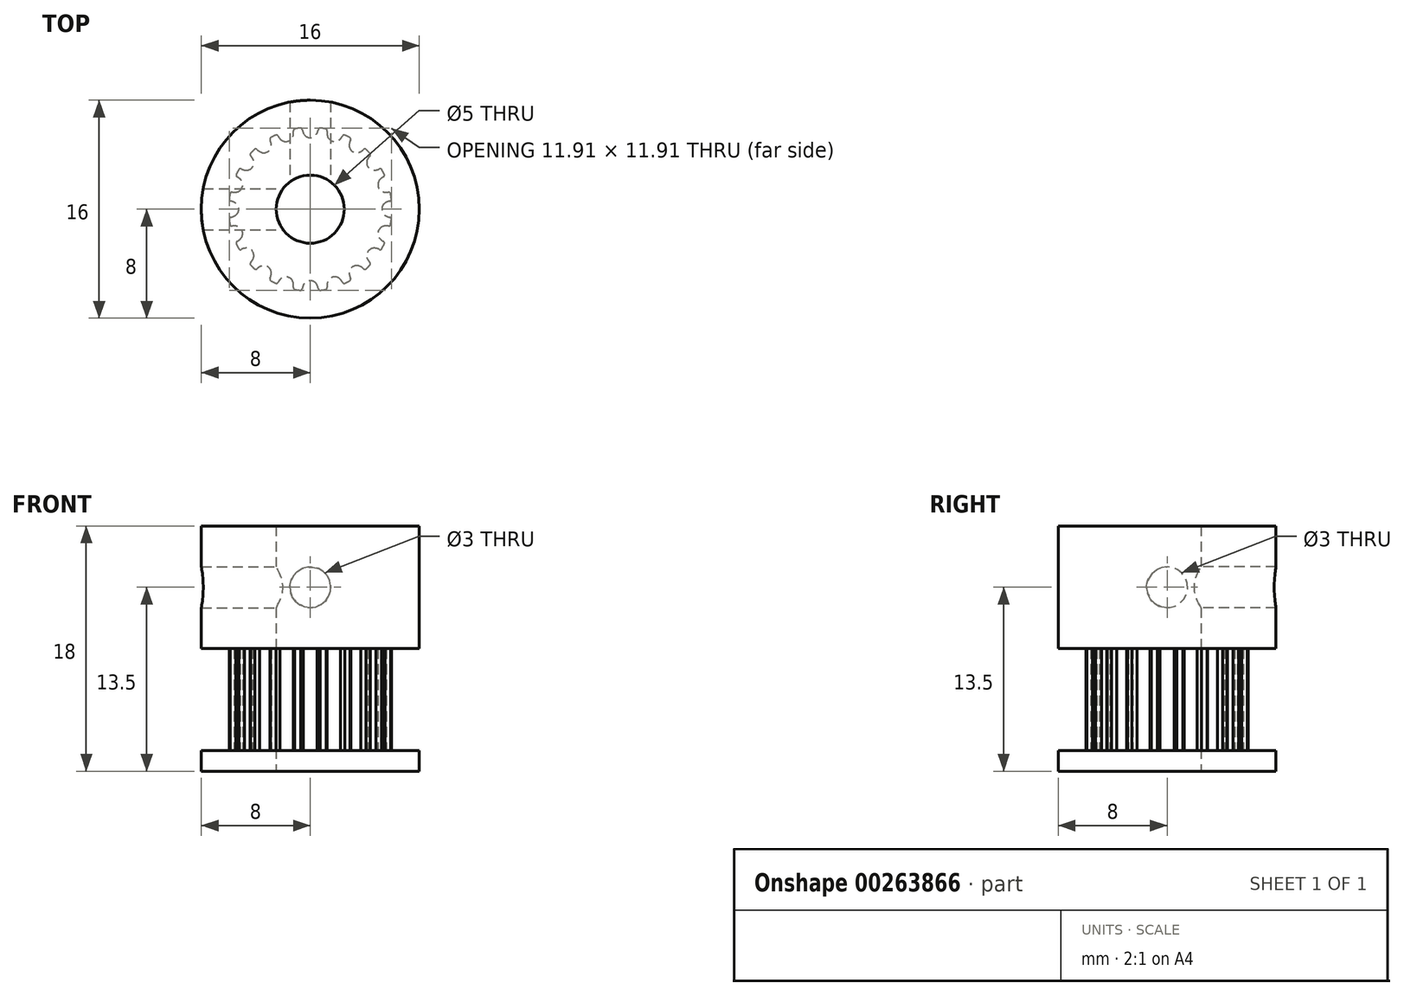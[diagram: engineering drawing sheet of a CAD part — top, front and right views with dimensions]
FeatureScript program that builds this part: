
annotation { "Feature Type Name" : "Feature", "Feature Type Description" : "" }
export const myFeature = defineFeature(function(context is Context, id is Id, definition is map)
    precondition{}
    {
        {
            var Q0;
            Q0=qCreatedBy(makeId("Top.planeOp"),FACE);
            var sketch = newSketch(context, id + "F0", { "sketchPlane" : qUnion([Q0])});
            skLineSegment(sketch, "E0", {"start": v(-19.17, 17.78) * mm, "end": v(-18.17, 17.78) * mm});
            skLineSegment(sketch, "E1", {"start": v(-18.17, 17.78) * mm, "end": v(-18.17, 18.4) * mm});
            skArc(sketch, "E2", {"start": v(-18.67, 18.85) * mm, "mid": v(-18.88, 19.07) * mm, "end": v(-19.17, 19.16) * mm});
            skArc(sketch, "E3", {"start": v(-18.58, 18.54) * mm, "mid": v(-18.61, 18.7) * mm, "end": v(-18.67, 18.85) * mm});
            skArc(sketch, "E4", {"start": v(-18.58, 18.54) * mm, "mid": v(-18.53, 18.44) * mm, "end": v(-18.43, 18.4) * mm});
            skLineSegment(sketch, "E5", {"start": v(-18.43, 18.4) * mm, "end": v(-18.17, 18.4) * mm});
            skArc(sketch, "E6.0.MirrorCS", {"start": v(-19.67, 18.85) * mm, "mid": v(-19.47, 19.07) * mm, "end": v(-19.17, 19.16) * mm});
            skArc(sketch, "E7.0.MirrorCS", {"start": v(-19.76, 18.54) * mm, "mid": v(-19.73, 18.7) * mm, "end": v(-19.67, 18.85) * mm});
            skArc(sketch, "E8.0.MirrorCS", {"start": v(-19.76, 18.54) * mm, "mid": v(-19.81, 18.44) * mm, "end": v(-19.91, 18.4) * mm});
            skLineSegment(sketch, "E9.0.MirrorCS", {"start": v(-19.91, 18.4) * mm, "end": v(-20.17, 18.4) * mm});
            skLineSegment(sketch, "E10.0.MirrorCS", {"start": v(-20.17, 17.78) * mm, "end": v(-20.17, 18.4) * mm});
            skLineSegment(sketch, "E11.0.MirrorCS", {"start": v(-19.17, 17.78) * mm, "end": v(-20.17, 17.78) * mm});
            skLineSegment(sketch, "E12.direction1", {"start": v(-20.17, 17.78) * mm, "end": v(-18.17, 17.78) * mm, "construction": true});
            skLineSegment(sketch, "E13", {"start": v(-20.17, 18.15) * mm, "end": v(-18.17, 18.15) * mm, "construction": true});
            skPoint(sketch, "E14", {"position": v(0, -5.25) * mm});
            skArc(sketch, "E15", {"start": v(0.51, -5.6) * mm, "mid": v(0, -5.25) * mm, "end": v(-0.51, -5.6) * mm});
            skArc(sketch, "E16", {"start": v(-0.51, -5.6) * mm, "mid": v(-0.56, -5.71) * mm, "end": v(-0.59, -5.83) * mm});
            skArc(sketch, "E17", {"start": v(0.59, -5.83) * mm, "mid": v(0.56, -5.71) * mm, "end": v(0.51, -5.6) * mm});
            skArc(sketch, "E18", {"start": v(0.72, -5.96) * mm, "mid": v(0.94, -5.93) * mm, "end": v(1.16, -5.89) * mm});
            skArc(sketch, "E19", {"start": v(0.59, -5.83) * mm, "mid": v(0.66, -5.94) * mm, "end": v(0.8, -5.95) * mm});
            skArc(sketch, "E20", {"start": v(-0.59, -5.83) * mm, "mid": v(-0.66, -5.94) * mm, "end": v(-0.8, -5.95) * mm});
            skArc(sketch, "E21.1.0", {"start": v(2.22, -5.16) * mm, "mid": v(1.62, -5) * mm, "end": v(1.24, -5.48) * mm});
            skPoint(sketch, "E21.1.1", {"position": v(1.62, -5) * mm});
            skArc(sketch, "E21.1.2", {"start": v(1.24, -5.48) * mm, "mid": v(1.23, -5.6) * mm, "end": v(1.24, -5.73) * mm});
            skArc(sketch, "E21.1.3", {"start": v(2.36, -5.37) * mm, "mid": v(2.47, -5.44) * mm, "end": v(2.6, -5.41) * mm});
            skArc(sketch, "E21.1.4", {"start": v(1.24, -5.73) * mm, "mid": v(1.2, -5.85) * mm, "end": v(1.08, -5.9) * mm});
            skArc(sketch, "E21.1.5", {"start": v(2.36, -5.37) * mm, "mid": v(2.3, -5.26) * mm, "end": v(2.22, -5.16) * mm});
            skArc(sketch, "E22.3.2.0", {"start": v(3.7, -4.22) * mm, "mid": v(3.09, -4.25) * mm, "end": v(2.87, -4.83) * mm});
            skPoint(sketch, "E22.4.2.0", {"position": v(3.09, -4.25) * mm});
            skArc(sketch, "E22.5.2.0", {"start": v(2.87, -4.83) * mm, "mid": v(2.9, -4.95) * mm, "end": v(2.95, -5.07) * mm});
            skArc(sketch, "E22.9.2.0", {"start": v(3.9, -4.37) * mm, "mid": v(4.03, -4.41) * mm, "end": v(4.14, -4.35) * mm});
            skArc(sketch, "E22.13.2.0", {"start": v(2.95, -5.07) * mm, "mid": v(2.95, -5.2) * mm, "end": v(2.85, -5.28) * mm});
            skArc(sketch, "E22.17.2.0", {"start": v(3.9, -4.37) * mm, "mid": v(3.81, -4.3) * mm, "end": v(3.7, -4.22) * mm});
            skArc(sketch, "E22.3.3.0", {"start": v(4.83, -2.87) * mm, "mid": v(4.25, -3.09) * mm, "end": v(4.22, -3.7) * mm});
            skPoint(sketch, "E22.4.3.0", {"position": v(4.25, -3.09) * mm});
            skArc(sketch, "E22.5.3.0", {"start": v(4.22, -3.7) * mm, "mid": v(4.3, -3.81) * mm, "end": v(4.37, -3.9) * mm});
            skArc(sketch, "E22.9.3.0", {"start": v(5.07, -2.95) * mm, "mid": v(5.2, -2.95) * mm, "end": v(5.28, -2.85) * mm});
            skArc(sketch, "E22.13.3.0", {"start": v(4.37, -3.9) * mm, "mid": v(4.41, -4.03) * mm, "end": v(4.35, -4.14) * mm});
            skArc(sketch, "E22.17.3.0", {"start": v(5.07, -2.95) * mm, "mid": v(4.95, -2.9) * mm, "end": v(4.83, -2.87) * mm});
            skArc(sketch, "E22.3.4.0", {"start": v(5.48, -1.24) * mm, "mid": v(5, -1.62) * mm, "end": v(5.16, -2.22) * mm});
            skPoint(sketch, "E22.4.4.0", {"position": v(5, -1.62) * mm});
            skArc(sketch, "E22.5.4.0", {"start": v(5.16, -2.22) * mm, "mid": v(5.26, -2.3) * mm, "end": v(5.37, -2.36) * mm});
            skArc(sketch, "E22.9.4.0", {"start": v(5.73, -1.24) * mm, "mid": v(5.85, -1.2) * mm, "end": v(5.9, -1.08) * mm});
            skArc(sketch, "E22.13.4.0", {"start": v(5.37, -2.36) * mm, "mid": v(5.44, -2.47) * mm, "end": v(5.41, -2.6) * mm});
            skArc(sketch, "E22.17.4.0", {"start": v(5.73, -1.24) * mm, "mid": v(5.6, -1.23) * mm, "end": v(5.48, -1.24) * mm});
            skArc(sketch, "E22.3.5.0", {"start": v(5.6, 0.51) * mm, "mid": v(5.25, 0) * mm, "end": v(5.6, -0.51) * mm});
            skPoint(sketch, "E22.4.5.0", {"position": v(5.25, 0) * mm});
            skArc(sketch, "E22.5.5.0", {"start": v(5.6, -0.51) * mm, "mid": v(5.71, -0.56) * mm, "end": v(5.83, -0.59) * mm});
            skArc(sketch, "E22.9.5.0", {"start": v(5.83, 0.59) * mm, "mid": v(5.94, 0.66) * mm, "end": v(5.95, 0.8) * mm});
            skArc(sketch, "E22.13.5.0", {"start": v(5.83, -0.59) * mm, "mid": v(5.94, -0.66) * mm, "end": v(5.95, -0.8) * mm});
            skArc(sketch, "E22.17.5.0", {"start": v(5.83, 0.59) * mm, "mid": v(5.71, 0.56) * mm, "end": v(5.6, 0.51) * mm});
            skArc(sketch, "E22.3.6.0", {"start": v(5.16, 2.22) * mm, "mid": v(5, 1.62) * mm, "end": v(5.48, 1.24) * mm});
            skPoint(sketch, "E22.4.6.0", {"position": v(5, 1.62) * mm});
            skArc(sketch, "E22.5.6.0", {"start": v(5.48, 1.24) * mm, "mid": v(5.6, 1.23) * mm, "end": v(5.73, 1.24) * mm});
            skArc(sketch, "E22.9.6.0", {"start": v(5.37, 2.36) * mm, "mid": v(5.44, 2.47) * mm, "end": v(5.41, 2.6) * mm});
            skArc(sketch, "E22.13.6.0", {"start": v(5.73, 1.24) * mm, "mid": v(5.85, 1.2) * mm, "end": v(5.9, 1.08) * mm});
            skArc(sketch, "E22.17.6.0", {"start": v(5.37, 2.36) * mm, "mid": v(5.26, 2.3) * mm, "end": v(5.16, 2.22) * mm});
            skArc(sketch, "E22.3.7.0", {"start": v(4.22, 3.7) * mm, "mid": v(4.25, 3.09) * mm, "end": v(4.83, 2.87) * mm});
            skPoint(sketch, "E22.4.7.0", {"position": v(4.25, 3.09) * mm});
            skArc(sketch, "E22.5.7.0", {"start": v(4.83, 2.87) * mm, "mid": v(4.95, 2.9) * mm, "end": v(5.07, 2.95) * mm});
            skArc(sketch, "E22.9.7.0", {"start": v(4.37, 3.9) * mm, "mid": v(4.41, 4.03) * mm, "end": v(4.35, 4.14) * mm});
            skArc(sketch, "E22.13.7.0", {"start": v(5.07, 2.95) * mm, "mid": v(5.2, 2.95) * mm, "end": v(5.28, 2.85) * mm});
            skArc(sketch, "E22.17.7.0", {"start": v(4.37, 3.9) * mm, "mid": v(4.3, 3.81) * mm, "end": v(4.22, 3.7) * mm});
            skArc(sketch, "E22.3.8.0", {"start": v(2.87, 4.83) * mm, "mid": v(3.09, 4.25) * mm, "end": v(3.7, 4.22) * mm});
            skPoint(sketch, "E22.4.8.0", {"position": v(3.09, 4.25) * mm});
            skArc(sketch, "E22.5.8.0", {"start": v(3.7, 4.22) * mm, "mid": v(3.81, 4.3) * mm, "end": v(3.9, 4.37) * mm});
            skArc(sketch, "E22.9.8.0", {"start": v(2.95, 5.07) * mm, "mid": v(2.95, 5.2) * mm, "end": v(2.85, 5.28) * mm});
            skArc(sketch, "E22.13.8.0", {"start": v(3.9, 4.37) * mm, "mid": v(4.03, 4.41) * mm, "end": v(4.14, 4.35) * mm});
            skArc(sketch, "E22.17.8.0", {"start": v(2.95, 5.07) * mm, "mid": v(2.9, 4.95) * mm, "end": v(2.87, 4.83) * mm});
            skArc(sketch, "E22.3.9.0", {"start": v(1.24, 5.48) * mm, "mid": v(1.62, 5) * mm, "end": v(2.22, 5.16) * mm});
            skPoint(sketch, "E22.4.9.0", {"position": v(1.62, 5) * mm});
            skArc(sketch, "E22.5.9.0", {"start": v(2.22, 5.16) * mm, "mid": v(2.3, 5.26) * mm, "end": v(2.36, 5.37) * mm});
            skArc(sketch, "E22.9.9.0", {"start": v(1.24, 5.73) * mm, "mid": v(1.2, 5.85) * mm, "end": v(1.08, 5.9) * mm});
            skArc(sketch, "E22.13.9.0", {"start": v(2.36, 5.37) * mm, "mid": v(2.47, 5.44) * mm, "end": v(2.6, 5.41) * mm});
            skArc(sketch, "E22.17.9.0", {"start": v(1.24, 5.73) * mm, "mid": v(1.23, 5.6) * mm, "end": v(1.24, 5.48) * mm});
            skArc(sketch, "E22.3.10.0", {"start": v(-0.51, 5.6) * mm, "mid": v(0, 5.25) * mm, "end": v(0.51, 5.6) * mm});
            skPoint(sketch, "E22.4.10.0", {"position": v(0, 5.25) * mm});
            skArc(sketch, "E22.5.10.0", {"start": v(0.51, 5.6) * mm, "mid": v(0.56, 5.71) * mm, "end": v(0.59, 5.83) * mm});
            skArc(sketch, "E22.9.10.0", {"start": v(-0.59, 5.83) * mm, "mid": v(-0.66, 5.94) * mm, "end": v(-0.8, 5.95) * mm});
            skArc(sketch, "E22.13.10.0", {"start": v(0.59, 5.83) * mm, "mid": v(0.66, 5.94) * mm, "end": v(0.8, 5.95) * mm});
            skArc(sketch, "E22.17.10.0", {"start": v(-0.59, 5.83) * mm, "mid": v(-0.56, 5.71) * mm, "end": v(-0.51, 5.6) * mm});
            skArc(sketch, "E22.3.11.0", {"start": v(-2.22, 5.16) * mm, "mid": v(-1.62, 5) * mm, "end": v(-1.24, 5.48) * mm});
            skPoint(sketch, "E22.4.11.0", {"position": v(-1.62, 5) * mm});
            skArc(sketch, "E22.5.11.0", {"start": v(-1.24, 5.48) * mm, "mid": v(-1.23, 5.6) * mm, "end": v(-1.24, 5.73) * mm});
            skArc(sketch, "E22.9.11.0", {"start": v(-2.36, 5.37) * mm, "mid": v(-2.47, 5.44) * mm, "end": v(-2.6, 5.41) * mm});
            skArc(sketch, "E22.13.11.0", {"start": v(-1.24, 5.73) * mm, "mid": v(-1.2, 5.85) * mm, "end": v(-1.08, 5.9) * mm});
            skArc(sketch, "E22.17.11.0", {"start": v(-2.36, 5.37) * mm, "mid": v(-2.3, 5.26) * mm, "end": v(-2.22, 5.16) * mm});
            skArc(sketch, "E22.3.12.0", {"start": v(-3.7, 4.22) * mm, "mid": v(-3.09, 4.25) * mm, "end": v(-2.87, 4.83) * mm});
            skPoint(sketch, "E22.4.12.0", {"position": v(-3.09, 4.25) * mm});
            skArc(sketch, "E22.5.12.0", {"start": v(-2.87, 4.83) * mm, "mid": v(-2.9, 4.95) * mm, "end": v(-2.95, 5.07) * mm});
            skArc(sketch, "E22.9.12.0", {"start": v(-3.9, 4.37) * mm, "mid": v(-4.03, 4.41) * mm, "end": v(-4.14, 4.35) * mm});
            skArc(sketch, "E22.13.12.0", {"start": v(-2.95, 5.07) * mm, "mid": v(-2.95, 5.2) * mm, "end": v(-2.85, 5.28) * mm});
            skArc(sketch, "E22.17.12.0", {"start": v(-3.9, 4.37) * mm, "mid": v(-3.81, 4.3) * mm, "end": v(-3.7, 4.22) * mm});
            skArc(sketch, "E22.3.13.0", {"start": v(-4.83, 2.87) * mm, "mid": v(-4.25, 3.09) * mm, "end": v(-4.22, 3.7) * mm});
            skPoint(sketch, "E22.4.13.0", {"position": v(-4.25, 3.09) * mm});
            skArc(sketch, "E22.5.13.0", {"start": v(-4.22, 3.7) * mm, "mid": v(-4.3, 3.81) * mm, "end": v(-4.37, 3.9) * mm});
            skArc(sketch, "E22.9.13.0", {"start": v(-5.07, 2.95) * mm, "mid": v(-5.2, 2.95) * mm, "end": v(-5.28, 2.85) * mm});
            skArc(sketch, "E22.13.13.0", {"start": v(-4.37, 3.9) * mm, "mid": v(-4.41, 4.03) * mm, "end": v(-4.35, 4.14) * mm});
            skArc(sketch, "E22.17.13.0", {"start": v(-5.07, 2.95) * mm, "mid": v(-4.95, 2.9) * mm, "end": v(-4.83, 2.87) * mm});
            skArc(sketch, "E22.3.14.0", {"start": v(-5.48, 1.24) * mm, "mid": v(-5, 1.62) * mm, "end": v(-5.16, 2.22) * mm});
            skPoint(sketch, "E22.4.14.0", {"position": v(-5, 1.62) * mm});
            skArc(sketch, "E22.5.14.0", {"start": v(-5.16, 2.22) * mm, "mid": v(-5.26, 2.3) * mm, "end": v(-5.37, 2.36) * mm});
            skArc(sketch, "E22.9.14.0", {"start": v(-5.73, 1.24) * mm, "mid": v(-5.85, 1.2) * mm, "end": v(-5.9, 1.08) * mm});
            skArc(sketch, "E22.13.14.0", {"start": v(-5.37, 2.36) * mm, "mid": v(-5.44, 2.47) * mm, "end": v(-5.41, 2.6) * mm});
            skArc(sketch, "E22.17.14.0", {"start": v(-5.73, 1.24) * mm, "mid": v(-5.6, 1.23) * mm, "end": v(-5.48, 1.24) * mm});
            skArc(sketch, "E22.3.15.0", {"start": v(-5.6, -0.51) * mm, "mid": v(-5.25, 0) * mm, "end": v(-5.6, 0.51) * mm});
            skPoint(sketch, "E22.4.15.0", {"position": v(-5.25, 0) * mm});
            skArc(sketch, "E22.5.15.0", {"start": v(-5.6, 0.51) * mm, "mid": v(-5.71, 0.56) * mm, "end": v(-5.83, 0.59) * mm});
            skArc(sketch, "E22.9.15.0", {"start": v(-5.83, -0.59) * mm, "mid": v(-5.94, -0.66) * mm, "end": v(-5.95, -0.8) * mm});
            skArc(sketch, "E22.13.15.0", {"start": v(-5.83, 0.59) * mm, "mid": v(-5.94, 0.66) * mm, "end": v(-5.95, 0.8) * mm});
            skArc(sketch, "E22.17.15.0", {"start": v(-5.83, -0.59) * mm, "mid": v(-5.71, -0.56) * mm, "end": v(-5.6, -0.51) * mm});
            skArc(sketch, "E22.3.16.0", {"start": v(-5.16, -2.22) * mm, "mid": v(-5, -1.62) * mm, "end": v(-5.48, -1.24) * mm});
            skPoint(sketch, "E22.4.16.0", {"position": v(-5, -1.62) * mm});
            skArc(sketch, "E22.5.16.0", {"start": v(-5.48, -1.24) * mm, "mid": v(-5.6, -1.23) * mm, "end": v(-5.73, -1.24) * mm});
            skArc(sketch, "E22.9.16.0", {"start": v(-5.37, -2.36) * mm, "mid": v(-5.44, -2.47) * mm, "end": v(-5.41, -2.6) * mm});
            skArc(sketch, "E22.13.16.0", {"start": v(-5.73, -1.24) * mm, "mid": v(-5.85, -1.2) * mm, "end": v(-5.9, -1.08) * mm});
            skArc(sketch, "E22.17.16.0", {"start": v(-5.37, -2.36) * mm, "mid": v(-5.26, -2.3) * mm, "end": v(-5.16, -2.22) * mm});
            skArc(sketch, "E22.3.17.0", {"start": v(-4.22, -3.7) * mm, "mid": v(-4.25, -3.09) * mm, "end": v(-4.83, -2.87) * mm});
            skPoint(sketch, "E22.4.17.0", {"position": v(-4.25, -3.09) * mm});
            skArc(sketch, "E22.5.17.0", {"start": v(-4.83, -2.87) * mm, "mid": v(-4.95, -2.9) * mm, "end": v(-5.07, -2.95) * mm});
            skArc(sketch, "E22.9.17.0", {"start": v(-4.37, -3.9) * mm, "mid": v(-4.41, -4.03) * mm, "end": v(-4.35, -4.14) * mm});
            skArc(sketch, "E22.13.17.0", {"start": v(-5.07, -2.95) * mm, "mid": v(-5.2, -2.95) * mm, "end": v(-5.28, -2.85) * mm});
            skArc(sketch, "E22.17.17.0", {"start": v(-4.37, -3.9) * mm, "mid": v(-4.3, -3.81) * mm, "end": v(-4.22, -3.7) * mm});
            skArc(sketch, "E22.3.18.0", {"start": v(-2.87, -4.83) * mm, "mid": v(-3.09, -4.25) * mm, "end": v(-3.7, -4.22) * mm});
            skPoint(sketch, "E22.4.18.0", {"position": v(-3.09, -4.25) * mm});
            skArc(sketch, "E22.5.18.0", {"start": v(-3.7, -4.22) * mm, "mid": v(-3.81, -4.3) * mm, "end": v(-3.9, -4.37) * mm});
            skArc(sketch, "E22.9.18.0", {"start": v(-2.95, -5.07) * mm, "mid": v(-2.95, -5.2) * mm, "end": v(-2.85, -5.28) * mm});
            skArc(sketch, "E22.13.18.0", {"start": v(-3.9, -4.37) * mm, "mid": v(-4.03, -4.41) * mm, "end": v(-4.14, -4.35) * mm});
            skArc(sketch, "E22.17.18.0", {"start": v(-2.95, -5.07) * mm, "mid": v(-2.9, -4.95) * mm, "end": v(-2.87, -4.83) * mm});
            skArc(sketch, "E22.3.19.0", {"start": v(-1.24, -5.48) * mm, "mid": v(-1.62, -5) * mm, "end": v(-2.22, -5.16) * mm});
            skPoint(sketch, "E22.4.19.0", {"position": v(-1.62, -5) * mm});
            skArc(sketch, "E22.5.19.0", {"start": v(-2.22, -5.16) * mm, "mid": v(-2.3, -5.26) * mm, "end": v(-2.36, -5.37) * mm});
            skArc(sketch, "E22.9.19.0", {"start": v(-1.24, -5.73) * mm, "mid": v(-1.2, -5.85) * mm, "end": v(-1.08, -5.9) * mm});
            skArc(sketch, "E22.13.19.0", {"start": v(-2.36, -5.37) * mm, "mid": v(-2.47, -5.44) * mm, "end": v(-2.6, -5.41) * mm});
            skArc(sketch, "E22.17.19.0", {"start": v(-1.24, -5.73) * mm, "mid": v(-1.23, -5.6) * mm, "end": v(-1.24, -5.48) * mm});
            skArc(sketch, "E23.trimOffspring", {"start": v(2.52, -5.44) * mm, "mid": v(2.72, -5.35) * mm, "end": v(2.92, -5.24) * mm});
            skArc(sketch, "E24.trimOffspring", {"start": v(4.08, -4.4) * mm, "mid": v(4.24, -4.24) * mm, "end": v(4.4, -4.08) * mm});
            skArc(sketch, "E25.trimOffspring", {"start": v(5.24, -2.92) * mm, "mid": v(5.33, -2.76) * mm, "end": v(5.41, -2.6) * mm});
            skArc(sketch, "E26.trimOffspring", {"start": v(5.89, -1.16) * mm, "mid": v(5.93, -0.94) * mm, "end": v(5.96, -0.72) * mm});
            skArc(sketch, "E27.trimOffspring", {"start": v(5.44, 2.52) * mm, "mid": v(5.35, 2.72) * mm, "end": v(5.24, 2.92) * mm});
            skArc(sketch, "E28.trimOffspring", {"start": v(4.4, 4.08) * mm, "mid": v(4.24, 4.24) * mm, "end": v(4.08, 4.4) * mm});
            skArc(sketch, "E29.trimOffspring", {"start": v(5.96, 0.72) * mm, "mid": v(5.93, 0.94) * mm, "end": v(5.89, 1.16) * mm});
            skArc(sketch, "E30.trimOffspring", {"start": v(2.92, 5.24) * mm, "mid": v(2.72, 5.35) * mm, "end": v(2.52, 5.44) * mm});
            skArc(sketch, "E31.trimOffspring", {"start": v(1.16, 5.89) * mm, "mid": v(0.94, 5.93) * mm, "end": v(0.72, 5.96) * mm});
            skArc(sketch, "E32.trimOffspring", {"start": v(-0.72, 5.96) * mm, "mid": v(-0.94, 5.93) * mm, "end": v(-1.16, 5.89) * mm});
            skArc(sketch, "E33.trimOffspring", {"start": v(-2.52, 5.44) * mm, "mid": v(-2.72, 5.35) * mm, "end": v(-2.92, 5.24) * mm});
            skArc(sketch, "E34.trimOffspring", {"start": v(-4.08, 4.4) * mm, "mid": v(-4.24, 4.24) * mm, "end": v(-4.4, 4.08) * mm});
            skArc(sketch, "E35.trimOffspring", {"start": v(-5.24, 2.92) * mm, "mid": v(-5.35, 2.72) * mm, "end": v(-5.44, 2.52) * mm});
            skArc(sketch, "E36.trimOffspring", {"start": v(-5.89, 1.16) * mm, "mid": v(-5.93, 0.94) * mm, "end": v(-5.96, 0.72) * mm});
            skArc(sketch, "E37.trimOffspring", {"start": v(-5.96, -0.72) * mm, "mid": v(-5.93, -0.94) * mm, "end": v(-5.89, -1.16) * mm});
            skArc(sketch, "E38.trimOffspring", {"start": v(-5.44, -2.52) * mm, "mid": v(-5.35, -2.72) * mm, "end": v(-5.24, -2.92) * mm});
            skArc(sketch, "E39.trimOffspring", {"start": v(-4.4, -4.08) * mm, "mid": v(-4.24, -4.24) * mm, "end": v(-4.08, -4.4) * mm});
            skArc(sketch, "E40.trimOffspring", {"start": v(-2.92, -5.24) * mm, "mid": v(-2.72, -5.35) * mm, "end": v(-2.52, -5.44) * mm});
            skArc(sketch, "E41.trimOffspring", {"start": v(-1.16, -5.89) * mm, "mid": v(-0.94, -5.93) * mm, "end": v(-0.72, -5.96) * mm});
            skSolve(sketch);
        }
        {
            var Q0;
            Q0=makeQuery(id+"F0.imprint","IMPRINT",FACE,{"disambiguationData":[TD([[makeQuery(id+"F0.imprint","IMPRINT",EDGE,{"derivedFrom":sQuery(id+"F0.wireOp",EDGE,"E15")}),-1.0]])]});
            extrude(context, id + "F1", {"entities" : qUnion([Q0]), "depth" : 7.5 * mm});
        }
        {
            var Q0;
            Q0=makeQuery(id+"F1.opExtrude","CAP_FACE",FACE,{"disambiguationData":[OSD([sQuery(id+"F0.wireOp",EDGE,"E15"),sQuery(id+"F0.wireOp",EDGE,"E16"),sQuery(id+"F0.wireOp",EDGE,"E17"),sQuery(id+"F0.wireOp",EDGE,"E18"),sQuery(id+"F0.wireOp",EDGE,"E19"),sQuery(id+"F0.wireOp",EDGE,"E20"),sQuery(id+"F0.wireOp",EDGE,"E21.1.0"),sQuery(id+"F0.wireOp",EDGE,"E21.1.2"),sQuery(id+"F0.wireOp",EDGE,"E21.1.3"),sQuery(id+"F0.wireOp",EDGE,"E21.1.4"),sQuery(id+"F0.wireOp",EDGE,"E21.1.5"),sQuery(id+"F0.wireOp",EDGE,"E22.3.2.0"),sQuery(id+"F0.wireOp",EDGE,"E22.5.2.0"),sQuery(id+"F0.wireOp",EDGE,"E22.9.2.0"),sQuery(id+"F0.wireOp",EDGE,"E22.13.2.0"),sQuery(id+"F0.wireOp",EDGE,"E22.17.2.0"),sQuery(id+"F0.wireOp",EDGE,"E22.3.3.0"),sQuery(id+"F0.wireOp",EDGE,"E22.5.3.0"),sQuery(id+"F0.wireOp",EDGE,"E22.9.3.0"),sQuery(id+"F0.wireOp",EDGE,"E22.13.3.0"),sQuery(id+"F0.wireOp",EDGE,"E22.17.3.0"),sQuery(id+"F0.wireOp",EDGE,"E22.3.4.0"),sQuery(id+"F0.wireOp",EDGE,"E22.5.4.0"),sQuery(id+"F0.wireOp",EDGE,"E22.9.4.0"),sQuery(id+"F0.wireOp",EDGE,"E22.13.4.0"),sQuery(id+"F0.wireOp",EDGE,"E22.17.4.0"),sQuery(id+"F0.wireOp",EDGE,"E22.3.5.0"),sQuery(id+"F0.wireOp",EDGE,"E22.5.5.0"),sQuery(id+"F0.wireOp",EDGE,"E22.9.5.0"),sQuery(id+"F0.wireOp",EDGE,"E22.13.5.0"),sQuery(id+"F0.wireOp",EDGE,"E22.17.5.0"),sQuery(id+"F0.wireOp",EDGE,"E22.3.6.0"),sQuery(id+"F0.wireOp",EDGE,"E22.5.6.0"),sQuery(id+"F0.wireOp",EDGE,"E22.9.6.0"),sQuery(id+"F0.wireOp",EDGE,"E22.13.6.0"),sQuery(id+"F0.wireOp",EDGE,"E22.17.6.0"),sQuery(id+"F0.wireOp",EDGE,"E22.3.7.0"),sQuery(id+"F0.wireOp",EDGE,"E22.5.7.0"),sQuery(id+"F0.wireOp",EDGE,"E22.9.7.0"),sQuery(id+"F0.wireOp",EDGE,"E22.13.7.0"),sQuery(id+"F0.wireOp",EDGE,"E22.17.7.0"),sQuery(id+"F0.wireOp",EDGE,"E22.3.8.0"),sQuery(id+"F0.wireOp",EDGE,"E22.5.8.0"),sQuery(id+"F0.wireOp",EDGE,"E22.9.8.0"),sQuery(id+"F0.wireOp",EDGE,"E22.13.8.0"),sQuery(id+"F0.wireOp",EDGE,"E22.17.8.0"),sQuery(id+"F0.wireOp",EDGE,"E22.3.9.0"),sQuery(id+"F0.wireOp",EDGE,"E22.5.9.0"),sQuery(id+"F0.wireOp",EDGE,"E22.9.9.0"),sQuery(id+"F0.wireOp",EDGE,"E22.13.9.0"),sQuery(id+"F0.wireOp",EDGE,"E22.17.9.0"),sQuery(id+"F0.wireOp",EDGE,"E22.3.10.0"),sQuery(id+"F0.wireOp",EDGE,"E22.5.10.0"),sQuery(id+"F0.wireOp",EDGE,"E22.9.10.0"),sQuery(id+"F0.wireOp",EDGE,"E22.13.10.0"),sQuery(id+"F0.wireOp",EDGE,"E22.17.10.0"),sQuery(id+"F0.wireOp",EDGE,"E22.3.11.0"),sQuery(id+"F0.wireOp",EDGE,"E22.5.11.0"),sQuery(id+"F0.wireOp",EDGE,"E22.9.11.0"),sQuery(id+"F0.wireOp",EDGE,"E22.13.11.0"),sQuery(id+"F0.wireOp",EDGE,"E22.17.11.0"),sQuery(id+"F0.wireOp",EDGE,"E22.3.12.0"),sQuery(id+"F0.wireOp",EDGE,"E22.5.12.0"),sQuery(id+"F0.wireOp",EDGE,"E22.9.12.0"),sQuery(id+"F0.wireOp",EDGE,"E22.13.12.0"),sQuery(id+"F0.wireOp",EDGE,"E22.17.12.0"),sQuery(id+"F0.wireOp",EDGE,"E22.3.13.0"),sQuery(id+"F0.wireOp",EDGE,"E22.5.13.0"),sQuery(id+"F0.wireOp",EDGE,"E22.9.13.0"),sQuery(id+"F0.wireOp",EDGE,"E22.13.13.0"),sQuery(id+"F0.wireOp",EDGE,"E22.17.13.0"),sQuery(id+"F0.wireOp",EDGE,"E22.3.14.0"),sQuery(id+"F0.wireOp",EDGE,"E22.5.14.0"),sQuery(id+"F0.wireOp",EDGE,"E22.9.14.0"),sQuery(id+"F0.wireOp",EDGE,"E22.13.14.0"),sQuery(id+"F0.wireOp",EDGE,"E22.17.14.0"),sQuery(id+"F0.wireOp",EDGE,"E22.3.15.0"),sQuery(id+"F0.wireOp",EDGE,"E22.5.15.0"),sQuery(id+"F0.wireOp",EDGE,"E22.9.15.0"),sQuery(id+"F0.wireOp",EDGE,"E22.13.15.0"),sQuery(id+"F0.wireOp",EDGE,"E22.17.15.0"),sQuery(id+"F0.wireOp",EDGE,"E22.3.16.0"),sQuery(id+"F0.wireOp",EDGE,"E22.5.16.0"),sQuery(id+"F0.wireOp",EDGE,"E22.9.16.0"),sQuery(id+"F0.wireOp",EDGE,"E22.13.16.0"),sQuery(id+"F0.wireOp",EDGE,"E22.17.16.0"),sQuery(id+"F0.wireOp",EDGE,"E22.3.17.0"),sQuery(id+"F0.wireOp",EDGE,"E22.5.17.0"),sQuery(id+"F0.wireOp",EDGE,"E22.9.17.0"),sQuery(id+"F0.wireOp",EDGE,"E22.13.17.0"),sQuery(id+"F0.wireOp",EDGE,"E22.17.17.0"),sQuery(id+"F0.wireOp",EDGE,"E22.3.18.0"),sQuery(id+"F0.wireOp",EDGE,"E22.5.18.0"),sQuery(id+"F0.wireOp",EDGE,"E22.9.18.0"),sQuery(id+"F0.wireOp",EDGE,"E22.13.18.0"),sQuery(id+"F0.wireOp",EDGE,"E22.17.18.0"),sQuery(id+"F0.wireOp",EDGE,"E22.3.19.0"),sQuery(id+"F0.wireOp",EDGE,"E22.5.19.0"),sQuery(id+"F0.wireOp",EDGE,"E22.9.19.0"),sQuery(id+"F0.wireOp",EDGE,"E22.13.19.0"),sQuery(id+"F0.wireOp",EDGE,"E22.17.19.0"),sQuery(id+"F0.wireOp",EDGE,"E23.trimOffspring"),sQuery(id+"F0.wireOp",EDGE,"E24.trimOffspring"),sQuery(id+"F0.wireOp",EDGE,"E25.trimOffspring"),sQuery(id+"F0.wireOp",EDGE,"E26.trimOffspring"),sQuery(id+"F0.wireOp",EDGE,"E27.trimOffspring"),sQuery(id+"F0.wireOp",EDGE,"E28.trimOffspring"),sQuery(id+"F0.wireOp",EDGE,"E29.trimOffspring"),sQuery(id+"F0.wireOp",EDGE,"E30.trimOffspring"),sQuery(id+"F0.wireOp",EDGE,"E31.trimOffspring"),sQuery(id+"F0.wireOp",EDGE,"E32.trimOffspring"),sQuery(id+"F0.wireOp",EDGE,"E33.trimOffspring"),sQuery(id+"F0.wireOp",EDGE,"E34.trimOffspring"),sQuery(id+"F0.wireOp",EDGE,"E35.trimOffspring"),sQuery(id+"F0.wireOp",EDGE,"E36.trimOffspring"),sQuery(id+"F0.wireOp",EDGE,"E37.trimOffspring"),sQuery(id+"F0.wireOp",EDGE,"E38.trimOffspring"),sQuery(id+"F0.wireOp",EDGE,"E39.trimOffspring"),sQuery(id+"F0.wireOp",EDGE,"E40.trimOffspring"),sQuery(id+"F0.wireOp",EDGE,"E41.trimOffspring")])],"isStart":false});
            var sketch = newSketch(context, id + "F2", { "sketchPlane" : qUnion([Q0])});
            skCircle(sketch, "E42", {"center": v(0, 0) * mm, "radius": 8 * mm});
            skSolve(sketch);
        }
        {
            var Q0;
            Q0=qSketchRegion(id+"F2",true);
            extrude(context, id + "F3", {"entities" : qUnion([Q0]), "operationType" : NewBodyOperationType.ADD, "depth" : 9 * mm});
        }
        {
            var Q0;
            Q0=makeQuery(id+"F1.opExtrude","CAP_FACE",FACE,{"disambiguationData":[OSD([sQuery(id+"F0.wireOp",EDGE,"E15"),sQuery(id+"F0.wireOp",EDGE,"E16"),sQuery(id+"F0.wireOp",EDGE,"E17"),sQuery(id+"F0.wireOp",EDGE,"E18"),sQuery(id+"F0.wireOp",EDGE,"E19"),sQuery(id+"F0.wireOp",EDGE,"E20"),sQuery(id+"F0.wireOp",EDGE,"E21.1.0"),sQuery(id+"F0.wireOp",EDGE,"E21.1.2"),sQuery(id+"F0.wireOp",EDGE,"E21.1.3"),sQuery(id+"F0.wireOp",EDGE,"E21.1.4"),sQuery(id+"F0.wireOp",EDGE,"E21.1.5"),sQuery(id+"F0.wireOp",EDGE,"E22.3.2.0"),sQuery(id+"F0.wireOp",EDGE,"E22.5.2.0"),sQuery(id+"F0.wireOp",EDGE,"E22.9.2.0"),sQuery(id+"F0.wireOp",EDGE,"E22.13.2.0"),sQuery(id+"F0.wireOp",EDGE,"E22.17.2.0"),sQuery(id+"F0.wireOp",EDGE,"E22.3.3.0"),sQuery(id+"F0.wireOp",EDGE,"E22.5.3.0"),sQuery(id+"F0.wireOp",EDGE,"E22.9.3.0"),sQuery(id+"F0.wireOp",EDGE,"E22.13.3.0"),sQuery(id+"F0.wireOp",EDGE,"E22.17.3.0"),sQuery(id+"F0.wireOp",EDGE,"E22.3.4.0"),sQuery(id+"F0.wireOp",EDGE,"E22.5.4.0"),sQuery(id+"F0.wireOp",EDGE,"E22.9.4.0"),sQuery(id+"F0.wireOp",EDGE,"E22.13.4.0"),sQuery(id+"F0.wireOp",EDGE,"E22.17.4.0"),sQuery(id+"F0.wireOp",EDGE,"E22.3.5.0"),sQuery(id+"F0.wireOp",EDGE,"E22.5.5.0"),sQuery(id+"F0.wireOp",EDGE,"E22.9.5.0"),sQuery(id+"F0.wireOp",EDGE,"E22.13.5.0"),sQuery(id+"F0.wireOp",EDGE,"E22.17.5.0"),sQuery(id+"F0.wireOp",EDGE,"E22.3.6.0"),sQuery(id+"F0.wireOp",EDGE,"E22.5.6.0"),sQuery(id+"F0.wireOp",EDGE,"E22.9.6.0"),sQuery(id+"F0.wireOp",EDGE,"E22.13.6.0"),sQuery(id+"F0.wireOp",EDGE,"E22.17.6.0"),sQuery(id+"F0.wireOp",EDGE,"E22.3.7.0"),sQuery(id+"F0.wireOp",EDGE,"E22.5.7.0"),sQuery(id+"F0.wireOp",EDGE,"E22.9.7.0"),sQuery(id+"F0.wireOp",EDGE,"E22.13.7.0"),sQuery(id+"F0.wireOp",EDGE,"E22.17.7.0"),sQuery(id+"F0.wireOp",EDGE,"E22.3.8.0"),sQuery(id+"F0.wireOp",EDGE,"E22.5.8.0"),sQuery(id+"F0.wireOp",EDGE,"E22.9.8.0"),sQuery(id+"F0.wireOp",EDGE,"E22.13.8.0"),sQuery(id+"F0.wireOp",EDGE,"E22.17.8.0"),sQuery(id+"F0.wireOp",EDGE,"E22.3.9.0"),sQuery(id+"F0.wireOp",EDGE,"E22.5.9.0"),sQuery(id+"F0.wireOp",EDGE,"E22.9.9.0"),sQuery(id+"F0.wireOp",EDGE,"E22.13.9.0"),sQuery(id+"F0.wireOp",EDGE,"E22.17.9.0"),sQuery(id+"F0.wireOp",EDGE,"E22.3.10.0"),sQuery(id+"F0.wireOp",EDGE,"E22.5.10.0"),sQuery(id+"F0.wireOp",EDGE,"E22.9.10.0"),sQuery(id+"F0.wireOp",EDGE,"E22.13.10.0"),sQuery(id+"F0.wireOp",EDGE,"E22.17.10.0"),sQuery(id+"F0.wireOp",EDGE,"E22.3.11.0"),sQuery(id+"F0.wireOp",EDGE,"E22.5.11.0"),sQuery(id+"F0.wireOp",EDGE,"E22.9.11.0"),sQuery(id+"F0.wireOp",EDGE,"E22.13.11.0"),sQuery(id+"F0.wireOp",EDGE,"E22.17.11.0"),sQuery(id+"F0.wireOp",EDGE,"E22.3.12.0"),sQuery(id+"F0.wireOp",EDGE,"E22.5.12.0"),sQuery(id+"F0.wireOp",EDGE,"E22.9.12.0"),sQuery(id+"F0.wireOp",EDGE,"E22.13.12.0"),sQuery(id+"F0.wireOp",EDGE,"E22.17.12.0"),sQuery(id+"F0.wireOp",EDGE,"E22.3.13.0"),sQuery(id+"F0.wireOp",EDGE,"E22.5.13.0"),sQuery(id+"F0.wireOp",EDGE,"E22.9.13.0"),sQuery(id+"F0.wireOp",EDGE,"E22.13.13.0"),sQuery(id+"F0.wireOp",EDGE,"E22.17.13.0"),sQuery(id+"F0.wireOp",EDGE,"E22.3.14.0"),sQuery(id+"F0.wireOp",EDGE,"E22.5.14.0"),sQuery(id+"F0.wireOp",EDGE,"E22.9.14.0"),sQuery(id+"F0.wireOp",EDGE,"E22.13.14.0"),sQuery(id+"F0.wireOp",EDGE,"E22.17.14.0"),sQuery(id+"F0.wireOp",EDGE,"E22.3.15.0"),sQuery(id+"F0.wireOp",EDGE,"E22.5.15.0"),sQuery(id+"F0.wireOp",EDGE,"E22.9.15.0"),sQuery(id+"F0.wireOp",EDGE,"E22.13.15.0"),sQuery(id+"F0.wireOp",EDGE,"E22.17.15.0"),sQuery(id+"F0.wireOp",EDGE,"E22.3.16.0"),sQuery(id+"F0.wireOp",EDGE,"E22.5.16.0"),sQuery(id+"F0.wireOp",EDGE,"E22.9.16.0"),sQuery(id+"F0.wireOp",EDGE,"E22.13.16.0"),sQuery(id+"F0.wireOp",EDGE,"E22.17.16.0"),sQuery(id+"F0.wireOp",EDGE,"E22.3.17.0"),sQuery(id+"F0.wireOp",EDGE,"E22.5.17.0"),sQuery(id+"F0.wireOp",EDGE,"E22.9.17.0"),sQuery(id+"F0.wireOp",EDGE,"E22.13.17.0"),sQuery(id+"F0.wireOp",EDGE,"E22.17.17.0"),sQuery(id+"F0.wireOp",EDGE,"E22.3.18.0"),sQuery(id+"F0.wireOp",EDGE,"E22.5.18.0"),sQuery(id+"F0.wireOp",EDGE,"E22.9.18.0"),sQuery(id+"F0.wireOp",EDGE,"E22.13.18.0"),sQuery(id+"F0.wireOp",EDGE,"E22.17.18.0"),sQuery(id+"F0.wireOp",EDGE,"E22.3.19.0"),sQuery(id+"F0.wireOp",EDGE,"E22.5.19.0"),sQuery(id+"F0.wireOp",EDGE,"E22.9.19.0"),sQuery(id+"F0.wireOp",EDGE,"E22.13.19.0"),sQuery(id+"F0.wireOp",EDGE,"E22.17.19.0"),sQuery(id+"F0.wireOp",EDGE,"E23.trimOffspring"),sQuery(id+"F0.wireOp",EDGE,"E24.trimOffspring"),sQuery(id+"F0.wireOp",EDGE,"E25.trimOffspring"),sQuery(id+"F0.wireOp",EDGE,"E26.trimOffspring"),sQuery(id+"F0.wireOp",EDGE,"E27.trimOffspring"),sQuery(id+"F0.wireOp",EDGE,"E28.trimOffspring"),sQuery(id+"F0.wireOp",EDGE,"E29.trimOffspring"),sQuery(id+"F0.wireOp",EDGE,"E30.trimOffspring"),sQuery(id+"F0.wireOp",EDGE,"E31.trimOffspring"),sQuery(id+"F0.wireOp",EDGE,"E32.trimOffspring"),sQuery(id+"F0.wireOp",EDGE,"E33.trimOffspring"),sQuery(id+"F0.wireOp",EDGE,"E34.trimOffspring"),sQuery(id+"F0.wireOp",EDGE,"E35.trimOffspring"),sQuery(id+"F0.wireOp",EDGE,"E36.trimOffspring"),sQuery(id+"F0.wireOp",EDGE,"E37.trimOffspring"),sQuery(id+"F0.wireOp",EDGE,"E38.trimOffspring"),sQuery(id+"F0.wireOp",EDGE,"E39.trimOffspring"),sQuery(id+"F0.wireOp",EDGE,"E40.trimOffspring"),sQuery(id+"F0.wireOp",EDGE,"E41.trimOffspring")])],"isStart":true});
            var sketch = newSketch(context, id + "F4", { "sketchPlane" : qUnion([Q0])});
            skCircle(sketch, "E43", {"center": v(0, 0) * mm, "radius": 8 * mm});
            skSolve(sketch);
        }
        {
            var Q0;
            Q0=qSketchRegion(id+"F4",true);
            extrude(context, id + "F5", {"entities" : qUnion([Q0]), "operationType" : NewBodyOperationType.ADD, "depth" : 1.5 * mm});
        }
        {
            var Q0;
            Q0=makeQuery(id+"F5.opExtrude","CAP_FACE",FACE,{"disambiguationData":[OSD([sQuery(id+"F4.wireOp",EDGE,"E43")])],"isStart":false});
            var sketch = newSketch(context, id + "F6", { "sketchPlane" : qUnion([Q0])});
            skCircle(sketch, "E44", {"center": v(0, 0) * mm, "radius": 2.5 * mm});
            skSolve(sketch);
        }
        {
            var Q0;
            Q0=qSketchRegion(id+"F6",true);
            extrude(context, id + "F7", {"entities" : qUnion([Q0]), "operationType" : NewBodyOperationType.REMOVE, "endBound" : BoundingType.THROUGH_ALL, "oppositeDirection" : true, "depth" : 25 * mm});
        }
        {
            var Q0;
            Q0=qCreatedBy(makeId("Right.planeOp"),FACE);
            var sketch = newSketch(context, id + "F8", { "sketchPlane" : qUnion([Q0])});
            skCircle(sketch, "E45", {"center": v(0, 12) * mm, "radius": 1.5 * mm});
            skSolve(sketch);
        }
        {
            var Q0;
            Q0=qSketchRegion(id+"F8",true);
            extrude(context, id + "F9", {"entities" : qUnion([Q0]), "operationType" : NewBodyOperationType.REMOVE, "endBound" : BoundingType.THROUGH_ALL, "oppositeDirection" : true, "depth" : 25 * mm});
        }
        {
            var Q0;
            Q0=qCreatedBy(makeId("Front.planeOp"),FACE);
            var sketch = newSketch(context, id + "F10", { "sketchPlane" : qUnion([Q0])});
            skCircle(sketch, "E46", {"center": v(0, 12) * mm, "radius": 1.5 * mm});
            skSolve(sketch);
        }
        {
            var Q0;
            Q0=qSketchRegion(id+"F10",true);
            extrude(context, id + "F11", {"entities" : qUnion([Q0]), "operationType" : NewBodyOperationType.REMOVE, "endBound" : BoundingType.THROUGH_ALL, "oppositeDirection" : true, "depth" : 25 * mm});
        }
    });
